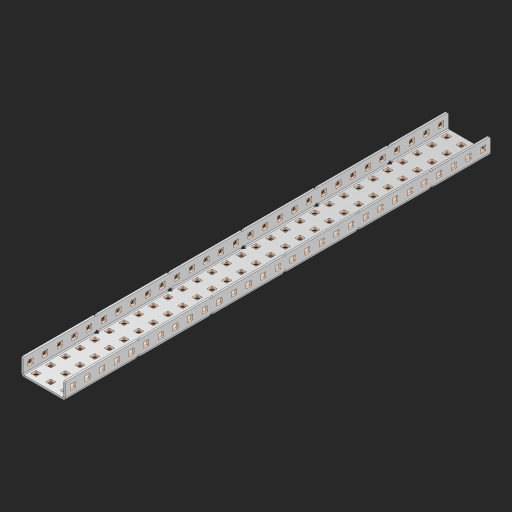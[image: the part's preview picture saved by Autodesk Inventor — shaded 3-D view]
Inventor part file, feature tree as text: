
AUTODESK INVENTOR PART (.ipt)
format: ipt  version: 2023 (Build 270158000, 158)  size: 1,778,176 bytes
history: native  units: in
note: dims shown in document units (in); Inventor stores cm internally (conversion verified against a paired STEP export)
features: other x150, extrude x144, sheet_metal_op x10, sketch x8, mirror x1, pattern_linear x1, chamfer x1
ambient origin geometry x8: Origin, YZ Plane, XZ Plane, XY Plane, X Axis, Y Axis, Z Axis, Center Point
bodies: Solid1 (feature_tree), Body (feature_tree)
feature tree (315):
  other  "Flange Pattern Plane"
  sheet_metal_op  "Flange Pattern"
  sheet_metal_op  "Body Pattern"
  other  "Arc Length"
  mirror  "Notch Mirror"
  pattern_linear  "Notch Pattern"  Spacing1=0.25in  [1 undecoded]
  chamfer  "End Chamfer"
  extrude  "Half Cut"  Depth=0.0625in
  sketch  "Sketch1"  dims[d0=1.5in]
  other  "Plate1"
  sketch  "Sketch2"  dims[d1=14.5in]
  other  "Plate2"
  sheet_metal_op  "Bend1"
  sheet_metal_op  "Corner1"
  sketch  "Sketch3"  dims[d2=0.0625in]
  other  "Flange Pattern Sketch"
  sketch  "Sketch7"  dims[d3=0.0625in]
  other  "Srf1"
  other  "Srf2"
  sketch  "Sketch8"  dims[d4=0.0312in]
  sketch  "Sketch9"  dims[d5=0.125in]
  other  "Srf91"
  sheet_metal_op  "Body Pattern Sketch"
  other  "Srf92"
  sketch  "Sketch13"  dims[d6=0.0625in]
  sketch  "Sketch14"  dims[d7=0.5in d8=90.0deg d9=0.0312in d10=0.25in d11=0.0625in d12=0.0625in d16=0.182in d17=0.02in d18=0.0625in d19=0.0in d20=0.25in d21=0.25in d46=0.172in d47=1.0in d48=0.0in d49=0.182in d50=0.02in d51=0.25in d52=0.25in d53=0.0625in d54=0.0in d55=0.172in d56=1.0in d57=0.0in d60=11.4173in d62=0.5in d63=1.1811in d65=0.5in d85=0.1473in d86=0.1782in d88=0.04in d89=0.0625in d90=0.0in d91=0.04in d92=0.0491in d95=2.5in d96=0.04in d97=0.25in d98=45.0deg d101=0.0in d102=2.497in d131=1.5in d132=11.4173in d134=0.5in d139=0.5in]
  other  "Srf856"
  other  "Srf1310"
  other  "Srf1311"
  other  "Srf1312"
  other  "Srf1376"
  other  "Srf1377"
  other  "Srf1728"
  other  "Srf1755"
  other  "Srf1878"
  other  "Srf1879"
  other  "Srf1880"
  other  "Srf1881"
  other  "Srf1882"
  other  "Srf1883"
  other  "Srf1884"
  other  "Srf1885"
  other  "Srf1886"
  other  "Srf1887"
  other  "Srf1888"
  other  "Srf1889"
  other  "Srf1890"
  other  "Srf1891"
  other  "Srf1892"
  other  "Srf1893"
  other  "Srf1894"
  other  "Srf1895"
  other  "Srf1896"
  other  "Srf1897"
  other  "Srf1898"
  other  "Srf1899"
  other  "Srf1900"
  other  "Srf1901"
  other  "Srf1902"
  other  "Srf1903"
  other  "Srf1904"
  other  "Srf1905"
  other  "Srf1906"
  other  "Srf1907"
  other  "Srf1908"
  other  "Srf1909"
  other  "Srf1910"
  other  "Srf1911"
  other  "Srf1912"
  other  "Srf1913"
  other  "Srf1914"
  other  "Srf1915"
  other  "Srf1916"
  other  "Srf1917"
  other  "Srf1918"
  other  "Srf1919"
  other  "Srf1920"
  other  "Srf1921"
  other  "Srf1922"
  other  "Srf1923"
  other  "Srf1924"
  other  "Srf1925"
  other  "Srf1926"
  other  "Srf1927"
  other  "Srf1928"
  other  "Srf1929"
  other  "Srf1942"
  other  "Srf1943"
  other  "Srf1944"
  other  "Srf1945"
  other  "Srf1946"
  other  "Srf1947"
  other  "Srf1948"
  other  "Srf1949"
  other  "Srf1950"
  other  "Srf1951"
  other  "Srf1952"
  other  "Srf1953"
  other  "Srf1954"
  other  "Srf1955"
  other  "Srf1956"
  other  "Srf1957"
  other  "Srf1958"
  other  "Srf1959"
  other  "Srf1960"
  other  "Srf1961"
  other  "Srf1962"
  other  "Srf1963"
  other  "Srf1964"
  other  "Srf1965"
  other  "Srf1966"
  other  "Srf1967"
  other  "Srf1968"
  other  "Srf1969"
  other  "Srf1970"
  other  "Srf1971"
  other  "Srf1972"
  other  "Srf1973"
  other  "Srf1974"
  other  "Srf1975"
  other  "Srf1976"
  other  "Srf1977"
  other  "Srf1978"
  other  "Srf1979"
  other  "Srf1980"
  other  "Srf1981"
  other  "Srf1982"
  other  "Srf1983"
  other  "Srf1984"
  other  "Srf1985"
  other  "Srf1986"
  other  "Srf1987"
  other  "Srf1988"
  other  "Srf1989"
  other  "Srf1990"
  other  "Srf1991"
  other  "Srf1992"
  other  "Srf1993"
  other  "Srf1994"
  other  "Srf1995"
  other  "Srf1996"
  other  "Srf1997"
  other  "Srf1998"
  other  "Srf1999"
  other  "Srf2000"
  other  "Srf2001"
  other  "Srf2002"
  other  "Srf2003"
  other  "Srf2004"
  other  "Srf2005"
  other  "Srf2006"
  other  "Srf2007"
  other  "Srf2008"
  other  "Srf2009"
  other  "Srf2010"
  other  "Srf2011"
  other  "Srf2012"
  other  "Srf2013"
  other  "Srf2014"
  other  "Srf2015"
  other  "Srf2016"
  other  "Srf2017"
  other  "Srf2018"
  other  "Srf2019"
  other  "Srf2020"
  other  "Srf2021"
  other  "Srf2022"
  sheet_metal_op  "Flange Stamp"
  sheet_metal_op  "Flange Circle"
  sheet_metal_op  "Body Stamp"
  sheet_metal_op  "Body Circle"
  sheet_metal_op  "Notch"
  extrude  "ExtrusionSrf2"  Depth=0.0625in
  extrude  "ExtrusionSrf92"  Depth=1.5in
  extrude  "ExtrusionSrf856"  Depth=0.02in
  extrude  "ExtrusionSrf1310"  Depth=0.0625in
  extrude  "ExtrusionSrf1311"  TaperAngle=0.0deg  [1 undecoded]
  extrude  "ExtrusionSrf1312"  Depth=0.25in
  extrude  "ExtrusionSrf1376"  Depth=0.25in
  extrude  "ExtrusionSrf1377"  Depth=1.5in
  extrude  "ExtrusionSrf1728"  Depth=1.5in TaperAngle=0.0deg
  extrude  "ExtrusionSrf1755"  Depth=1.5in
  extrude  "ExtrusionSrf1878"  Depth=0.02in
  extrude  "ExtrusionSrf1879"  Depth=0.25in
  extrude  "ExtrusionSrf1880"  Depth=0.25in
  extrude  "ExtrusionSrf1881"  Depth=0.0625in
  extrude  "ExtrusionSrf1882"  TaperAngle=0.0deg  [1 undecoded]
  extrude  "ExtrusionSrf1883"  Depth=1.5in
  extrude  "ExtrusionSrf1884"  Depth=1.5in TaperAngle=0.0deg
  extrude  "ExtrusionSrf1885"  Depth=1.5in
  extrude  "ExtrusionSrf1886"  Depth=1.5in
  extrude  "ExtrusionSrf1887"  Depth=1.5in
  extrude  "ExtrusionSrf1888"  Depth=1.5in
  extrude  "ExtrusionSrf1889"  Depth=1.5in
  extrude  "ExtrusionSrf1890"  Depth=0.0625in
  extrude  "ExtrusionSrf1891"  TaperAngle=0.0deg  [1 undecoded]
  extrude  "ExtrusionSrf1892"  Depth=1.5in
  extrude  "ExtrusionSrf1893"  Depth=1.5in
  extrude  "ExtrusionSrf1894"  Depth=1.5in
  extrude  "ExtrusionSrf1895"  Depth=0.25in TaperAngle=45.0deg
  extrude  "ExtrusionSrf1896"  TaperAngle=0.0deg  [1 undecoded]
  extrude  "ExtrusionSrf1897"  Depth=1.5in
  extrude  "ExtrusionSrf1898"  Depth=1.5in
  extrude  "ExtrusionSrf1899"  Depth=1.5in
  extrude  "ExtrusionSrf1900"  Depth=1.5in
  extrude  "ExtrusionSrf1901"  Depth=1.5in
  extrude  "ExtrusionSrf1902"  [1 undecoded]
  extrude  "ExtrusionSrf1903"  [1 undecoded]
  extrude  "ExtrusionSrf1904"  [1 undecoded]
  extrude  "ExtrusionSrf1905"  [1 undecoded]
  extrude  "ExtrusionSrf1906"  [1 undecoded]
  extrude  "ExtrusionSrf1907"  [1 undecoded]
  extrude  "ExtrusionSrf1908"  [1 undecoded]
  extrude  "ExtrusionSrf1909"  [1 undecoded]
  extrude  "ExtrusionSrf1910"  [1 undecoded]
  extrude  "ExtrusionSrf1911"  [1 undecoded]
  extrude  "ExtrusionSrf1912"  [1 undecoded]
  extrude  "ExtrusionSrf1913"  [1 undecoded]
  extrude  "ExtrusionSrf1914"  [1 undecoded]
  extrude  "ExtrusionSrf1915"  [1 undecoded]
  extrude  "ExtrusionSrf1916"  [1 undecoded]
  extrude  "ExtrusionSrf1917"  [1 undecoded]
  extrude  "ExtrusionSrf1918"  [1 undecoded]
  extrude  "ExtrusionSrf1919"  [1 undecoded]
  extrude  "ExtrusionSrf1920"  [1 undecoded]
  extrude  "ExtrusionSrf1921"  [1 undecoded]
  extrude  "ExtrusionSrf1922"  [1 undecoded]
  extrude  "ExtrusionSrf1923"  [1 undecoded]
  extrude  "ExtrusionSrf1924"  [1 undecoded]
  extrude  "ExtrusionSrf1925"  [1 undecoded]
  extrude  "ExtrusionSrf1926"  [1 undecoded]
  extrude  "ExtrusionSrf1927"  [1 undecoded]
  extrude  "ExtrusionSrf1928"  [1 undecoded]
  extrude  "ExtrusionSrf1929"  [1 undecoded]
  extrude  "ExtrusionSrf1942"  [1 undecoded]
  extrude  "ExtrusionSrf1943"  [1 undecoded]
  extrude  "ExtrusionSrf1944"  [1 undecoded]
  extrude  "ExtrusionSrf1945"  [1 undecoded]
  extrude  "ExtrusionSrf1946"  [1 undecoded]
  extrude  "ExtrusionSrf1947"  [1 undecoded]
  extrude  "ExtrusionSrf1948"  [1 undecoded]
  extrude  "ExtrusionSrf1949"  [1 undecoded]
  extrude  "ExtrusionSrf1950"  [1 undecoded]
  extrude  "ExtrusionSrf1951"  [1 undecoded]
  extrude  "ExtrusionSrf1952"  [1 undecoded]
  extrude  "ExtrusionSrf1953"  [1 undecoded]
  extrude  "ExtrusionSrf1954"  [1 undecoded]
  extrude  "ExtrusionSrf1955"  [1 undecoded]
  extrude  "ExtrusionSrf1956"  [1 undecoded]
  extrude  "ExtrusionSrf1957"  [1 undecoded]
  extrude  "ExtrusionSrf1958"  [1 undecoded]
  extrude  "ExtrusionSrf1959"  [1 undecoded]
  extrude  "ExtrusionSrf1960"  [1 undecoded]
  extrude  "ExtrusionSrf1961"  [1 undecoded]
  extrude  "ExtrusionSrf1962"  [1 undecoded]
  extrude  "ExtrusionSrf1963"  [1 undecoded]
  extrude  "ExtrusionSrf1964"  [1 undecoded]
  extrude  "ExtrusionSrf1965"  [1 undecoded]
  extrude  "ExtrusionSrf1966"  [1 undecoded]
  extrude  "ExtrusionSrf1967"  [1 undecoded]
  extrude  "ExtrusionSrf1968"  [1 undecoded]
  extrude  "ExtrusionSrf1969"  [1 undecoded]
  extrude  "ExtrusionSrf1970"  [1 undecoded]
  extrude  "ExtrusionSrf1971"  [1 undecoded]
  extrude  "ExtrusionSrf1972"  [1 undecoded]
  extrude  "ExtrusionSrf1973"  [1 undecoded]
  extrude  "ExtrusionSrf1974"  [1 undecoded]
  extrude  "ExtrusionSrf1975"  [1 undecoded]
  extrude  "ExtrusionSrf1976"  [1 undecoded]
  extrude  "ExtrusionSrf1977"  [1 undecoded]
  extrude  "ExtrusionSrf1978"  [1 undecoded]
  extrude  "ExtrusionSrf1979"  [1 undecoded]
  extrude  "ExtrusionSrf1980"  [1 undecoded]
  extrude  "ExtrusionSrf1981"  [1 undecoded]
  extrude  "ExtrusionSrf1982"  [1 undecoded]
  extrude  "ExtrusionSrf1983"  [1 undecoded]
  extrude  "ExtrusionSrf1984"  [1 undecoded]
  extrude  "ExtrusionSrf1985"  [1 undecoded]
  extrude  "ExtrusionSrf1986"  [1 undecoded]
  extrude  "ExtrusionSrf1987"  [1 undecoded]
  extrude  "ExtrusionSrf1988"  [1 undecoded]
  extrude  "ExtrusionSrf1989"  [1 undecoded]
  extrude  "ExtrusionSrf1990"  [1 undecoded]
  extrude  "ExtrusionSrf1991"  [1 undecoded]
  extrude  "ExtrusionSrf1992"  [1 undecoded]
  extrude  "ExtrusionSrf1993"  [1 undecoded]
  extrude  "ExtrusionSrf1994"  [1 undecoded]
  extrude  "ExtrusionSrf1995"  [1 undecoded]
  extrude  "ExtrusionSrf1996"  [1 undecoded]
  extrude  "ExtrusionSrf1997"  [1 undecoded]
  extrude  "ExtrusionSrf1998"  [1 undecoded]
  extrude  "ExtrusionSrf1999"  [1 undecoded]
  extrude  "ExtrusionSrf2000"  [1 undecoded]
  extrude  "ExtrusionSrf2001"  [1 undecoded]
  extrude  "ExtrusionSrf2002"  [1 undecoded]
  extrude  "ExtrusionSrf2003"  [1 undecoded]
  extrude  "ExtrusionSrf2004"  [1 undecoded]
  extrude  "ExtrusionSrf2005"  [1 undecoded]
  extrude  "ExtrusionSrf2006"  [1 undecoded]
  extrude  "ExtrusionSrf2007"  [1 undecoded]
  extrude  "ExtrusionSrf2008"  [1 undecoded]
  extrude  "ExtrusionSrf2009"  [1 undecoded]
  extrude  "ExtrusionSrf2010"  [1 undecoded]
  extrude  "ExtrusionSrf2011"  [1 undecoded]
  extrude  "ExtrusionSrf2012"  [1 undecoded]
  extrude  "ExtrusionSrf2013"  [1 undecoded]
  extrude  "ExtrusionSrf2014"  [1 undecoded]
  extrude  "ExtrusionSrf2015"  [1 undecoded]
  extrude  "ExtrusionSrf2016"  [1 undecoded]
  extrude  "ExtrusionSrf2017"  [1 undecoded]
  extrude  "ExtrusionSrf2018"  [1 undecoded]
  extrude  "ExtrusionSrf2019"  [1 undecoded]
  extrude  "ExtrusionSrf2020"  [1 undecoded]
  extrude  "ExtrusionSrf2021"  [1 undecoded]
  extrude  "ExtrusionSrf2022"  [1 undecoded]
note: 114 required parameter values undecoded (feature->parameter linkage not recoverable at this tier; creation-order binding heuristic only, values carry confidence <= 0.55)
